# Revit family: Узел подпитки и предотвращения обратного потока 0305
name_source: partatom
category: Rohrzubehör
units: mm (PartAtom-declared; Revit-internal decimal feet)

## family parameters
Arbeitsebenenbasiert = Nein
Beim Laden mit Abzugskörper schneiden = Nein
Bemaßung runder Anschluss = Durchmesser verwenden
Gemeinsam genutzt = Nein
Immer vertikal = Ja
OmniClass-Nummer = 23.65.55.14
OmniClass-Titel = Valves for Liquid Services
Teiletyp = Unterbricht

## types (1)
- Узел подпитки и предотвращения обратного потока 0305
    D02 = 15.2 mm
    D03 = 14.4 mm  [stored 0.0472441 ft]
    D04 = 12.9 mm
    D05 = 10.6 mm  [stored 0.0347769 ft]
    D06 = 16 mm  [stored 0.0524934 ft]
    D07 = 22 mm  [stored 0.0721785 ft]
    D08 = 18 mm  [stored 0.0590551 ft]
    D09 = 13.5 mm
    D10 = 16.3 mm  [stored 0.0534777 ft]
    D11 = 23.7 mm  [stored 0.0777559 ft]
    D12 = 22.8 mm  [stored 0.0748031 ft]
    D13 = 19.2 mm  [stored 0.0629921 ft]
    D14 = 14.2 mm  [stored 0.0465879 ft]
    D15 = 12.2 mm
    D16 = 66.7 mm
    D17 = 66.5 mm
    D18 = 92.3 mm
    Hersteller = HERZ Armaturen Ges.m.b.H.
    L03 = 13 mm
    L04 = 10 mm  [stored 0.0328084 ft]
    L05 = 4.8 mm  [stored 0.015748 ft]
    L08 = 15.5 mm
    L09 = 26.2 mm
    L10 = 23.3 mm
    L11 = 4 mm  [stored 0.0131234 ft]
    L12 = 4.8 mm  [stored 0.015748 ft]
    L13 = 8.7 mm
    L14 = 30 mm  [stored 0.0984252 ft]
    L15 = 18.8 mm
    L16 = 70.5 mm
    L17 = 6.5 mm
    L18 = 8.7 mm
    L19 = 36.7 mm
    L20 = 12 mm  [stored 0.0393701 ft]
    L21 = 11 mm  [stored 0.0360892 ft]
    L22 = 22 mm  [stored 0.0721785 ft]
    L23 = 34 mm  [stored 0.111549 ft]
    L24 = 10.1 mm
    L25 = 28.6 mm
    L26 = 48.5 mm
    L27 = 44.5 mm
    L28 = 85.3 mm
    L29 = 28.8 mm  [stored 0.0944882 ft]
    R01 = 8 mm  [stored 0.0262467 ft]
    R02 = 7 mm  [stored 0.0229659 ft]
    R03 = 8.5 mm  [stored 0.0278871 ft]
    R04 = 7.5 mm  [stored 0.0246063 ft]
    R05 = 6.5 mm
    R06 = 7.3 mm
    R07 = 31 mm  [stored 0.101706 ft]
    R08 = 8.5 mm  [stored 0.0278871 ft]
    S03 = 40 mm
    S04 = 20 mm
    S05 = 8 mm  [stored 0.0262467 ft]
    S06 = 27 mm
    S07 = 75 mm
    S08 = 65 mm
    SCTWCODE = 04;12;02
    SCTWSEQ = AW;SBT_TYP_AW="104";2
    SC_NennweiteBerechnet = 0
    URL = www.herz-armaturen.ru
    Vorgabe-Ansicht = 0 mm  [stored 0 ft]
    W01 = 45.00°
    W02 = 80.00°
    Давление на выходе (регулируемое) = 0.5-3 bar
    Корпус = латунь, CW617N
    Макс. допустимая рабочая температура (кратковременно) = 85 °C
    Макс. рабочая температура = 65 °C
    Макс. рабочее давление = 1000000.0 Pa
    Область применения = Согласно EN 1717 задача узлов предотвращения обратного потока состоит в том, чтобы не допустить обратного оттока или всасывания загрязнённой воды в сеть питьевого водоснабжения.
Они устанавливаются в местах, где сеть питьевого водоснабжения соединяется с технической водой жёсткими или гибкими трубопроводами.
В основном эти узлы применяются в установках для умягчения, понижения кислотности, а также декарбонизации воды.
Кроме этого, узлы предотвращения обратного потока могут устанвливаться в дезинфицирующих системах или перед аппаратами химической очистки для предотвращения обратного потока химически загрязненной воды в систему питьевого водоснабжения.
    Положение при монтаже = горизонтальное
    Предварительная заводская настройка давления = 150000.0 Pa
    Примечание = В соответствии со статьей 33 Регламента REACH (Registration; Evaluation; Authorisation; Restriction of Chemicals) (EC № 1907/2006) мы обязаны указать, что свинец внесен в список SVHC (Substances of Very High Concern - вещества очень высокой важности) и весовой процент свинца во всех латунных компонентах заводского изготовления в наших изделиях, превышает 0,1 % (w/w) (CAS: 7439-92-1 / EINECS: 231-100-4).
Поскольку свинец является легирующим компонентом сплава, прямое негативное влияние исключается, и поэтому дополнительной информации о безопасном использовании не требуется.
    Среда = питьевая вода
    Уплотнение = EPDM

note: [stored X ft] marks values corroborated as IEEE doubles in the binary element streams (Revit-internal decimal feet)
